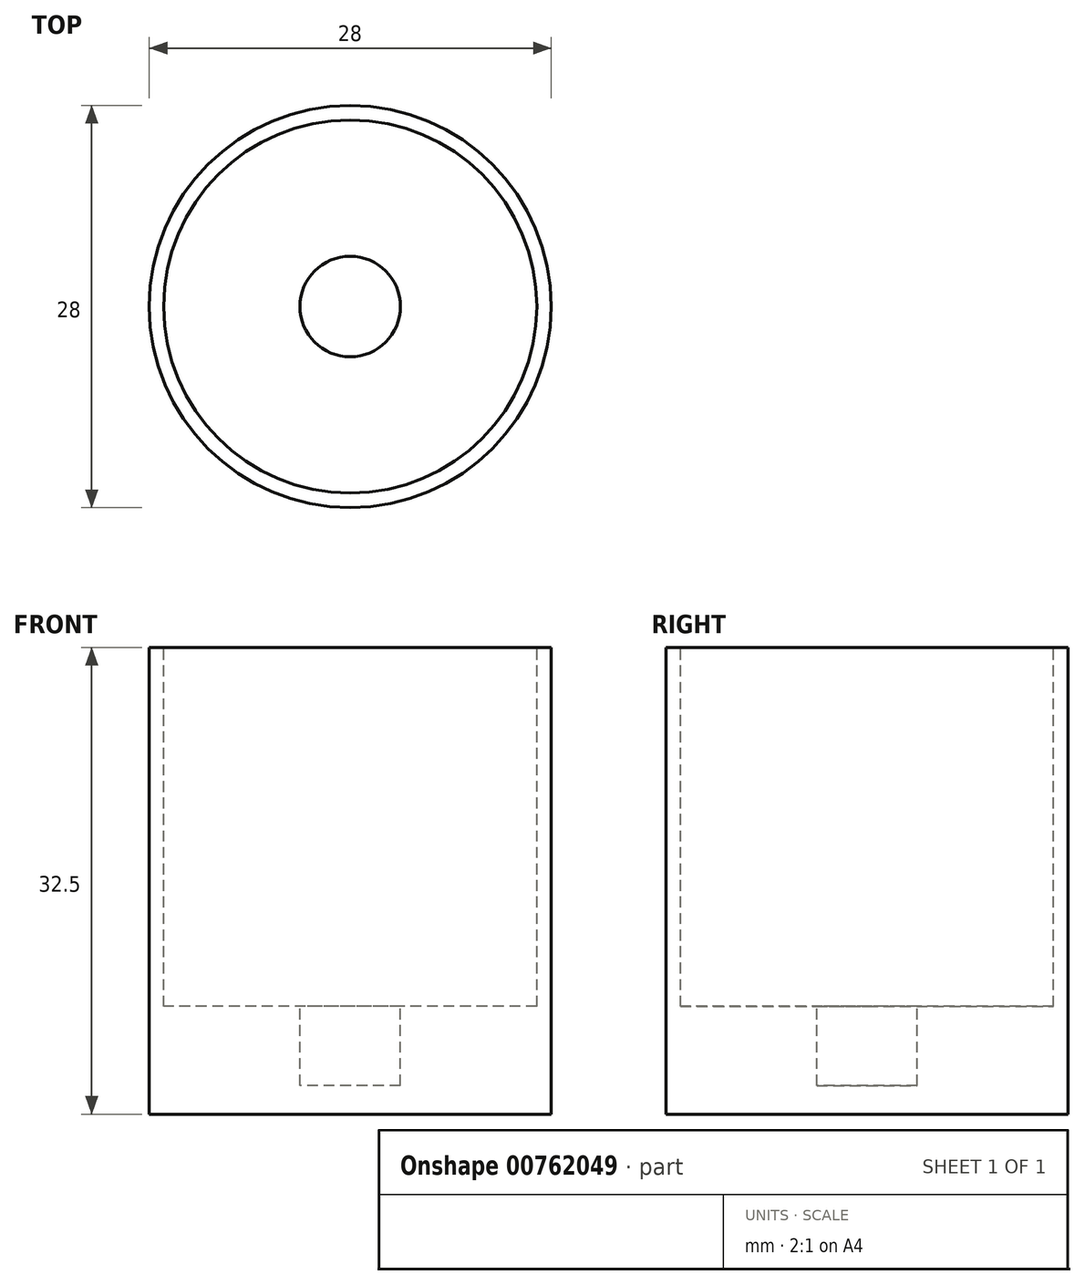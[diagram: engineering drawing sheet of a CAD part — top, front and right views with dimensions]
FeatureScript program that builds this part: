
annotation { "Feature Type Name" : "Feature", "Feature Type Description" : "" }
export const myFeature = defineFeature(function(context is Context, id is Id, definition is map)
    precondition{}
    {
        {
            var Q0;
            Q0=qCreatedBy(makeId("Front.planeOp"),FACE);
            var sketch = newSketch(context, id + "F0", { "sketchPlane" : qUnion([Q0])});
            skLineSegment(sketch, "E0", {"start": v(0, 0) * mm, "end": v(14, 0) * mm});
            skLineSegment(sketch, "E1", {"start": v(14, 0) * mm, "end": v(14, 32.5) * mm});
            skLineSegment(sketch, "E2", {"start": v(14, 32.5) * mm, "end": v(13, 32.5) * mm});
            skLineSegment(sketch, "E3", {"start": v(13, 32.5) * mm, "end": v(13, 7.5) * mm});
            skLineSegment(sketch, "E4", {"start": v(13, 7.5) * mm, "end": v(3.5, 7.5) * mm});
            skLineSegment(sketch, "E5", {"start": v(3.5, 7.5) * mm, "end": v(3.5, 2) * mm});
            skLineSegment(sketch, "E6", {"start": v(3.5, 2) * mm, "end": v(0, 2) * mm});
            skLineSegment(sketch, "E7", {"start": v(0, 2) * mm, "end": v(0, 0) * mm});
            skPoint(sketch, "E8.orphan", {"position": v(0, 83.55) * mm});
            skSolve(sketch);
        }
        {
            var Q0;
            Q0 = qSketchRegion(id + "F0", true);
            var Q1;
            Q1=sQuery(id+"F0.wireOp",EDGE,"E7");
            revolve(context, id + "F1", {"surfaceOperationType" : NewSurfaceOperationType.NEW, "entities" : qUnion([Q0]), "axis" : qUnion([Q1]), "revolveType" : RevolveType.FULL});
        }
    });
